# Revit family: 210_36edea14a2914841a884d0da290209
name_source: partatom
category: Mechanical Equipment
revit_build: Autodesk Revit 2018 (Build: 20170223_1515(x64)
units: mm (PartAtom-declared; Revit-internal decimal feet)

## family parameters
Always vertical = Yes
Classification = None
Cut with Voids When Loaded = No
Part Type = Breaks Into
Room Calculation Point = No
Round Connector Dimension = Use Diameter
Shared = No
Work Plane-Based = No

## types (1)
- 100-115462
    A1 = 34 mm
    A2 = 2 mm  [stored 0.00656168 ft]
    A3 = 9 mm  [stored 0.0295276 ft]
    AT2 = 88 mm
    AT3 = 83 mm
    CAT0 = Yes
    D = 100 mm
    DT2 = 50 mm  [stored 0.164042 ft]
    Description = Bathroom fan Pro7
    L2 = 25 mm  [stored 0.082021 ft]
    MC Product Code = 100-115462
    Manufacturer = Flexit
    QmdConnectorList = 201;D
    URL = www.flexit.no
    W = 500 mm
    magiPartTypeId = 210
    magiProductFamilyId = 36edea14a2914841a884d0da290209
    magiProductId = d831c4d33a6343e3a958dfc62a24aa

note: [stored X ft] marks values corroborated as IEEE doubles in the binary element streams (Revit-internal decimal feet)

## geometry (parser evidence)
native form markers: Sweep x2
no freeform markers — native parametric forms only
